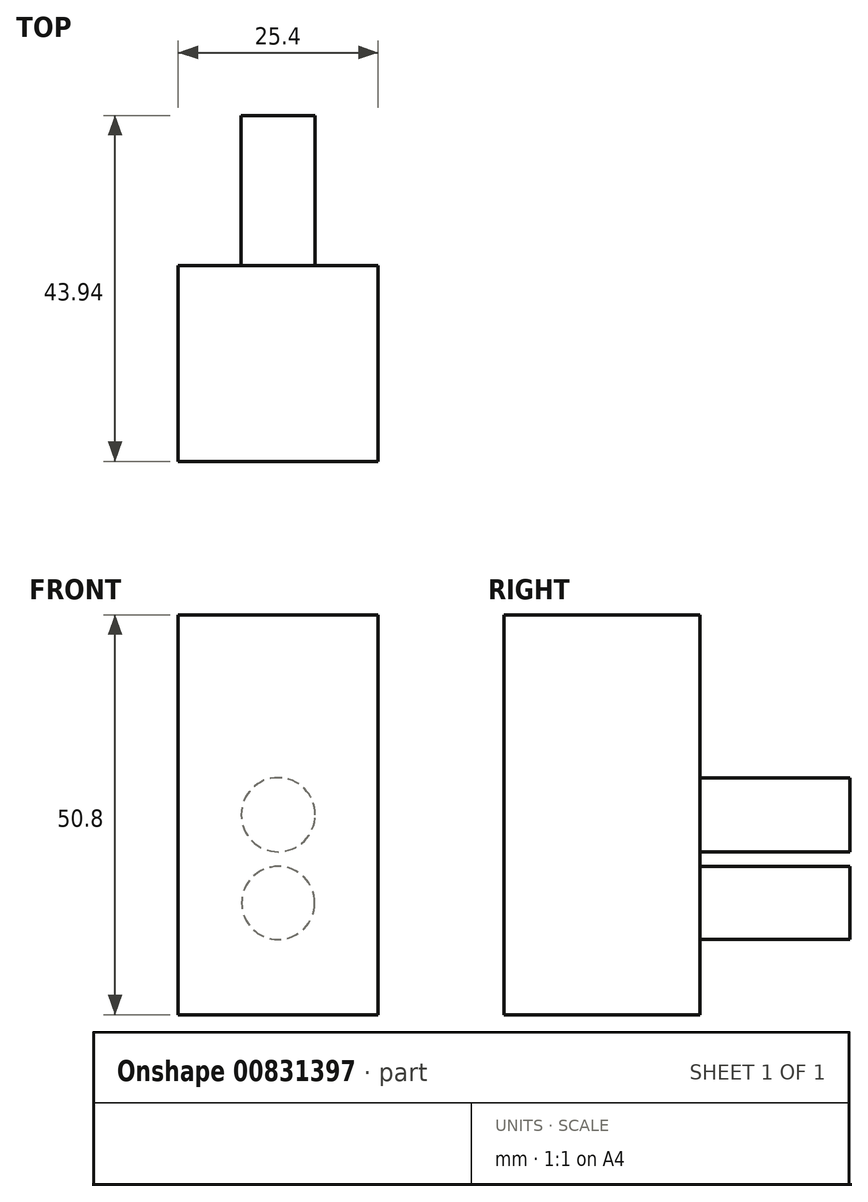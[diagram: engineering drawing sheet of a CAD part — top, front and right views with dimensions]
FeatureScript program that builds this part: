
annotation { "Feature Type Name" : "Feature", "Feature Type Description" : "" }
export const myFeature = defineFeature(function(context is Context, id is Id, definition is map)
    precondition{}
    {
        {
            var Q0;
            Q0=qCreatedBy(makeId("Front.planeOp"),FACE);
            var sketch = newSketch(context, id + "F0", { "sketchPlane" : qUnion([Q0])});
            skLineSegment(sketch, "E0.bottom", {"start": v(12.7, -25.4) * mm, "end": v(-12.7, -25.4) * mm});
            skLineSegment(sketch, "E0.top", {"start": v(12.7, 25.4) * mm, "end": v(-12.7, 25.4) * mm});
            skLineSegment(sketch, "E0.left", {"start": v(12.7, -25.4) * mm, "end": v(12.7, 25.4) * mm});
            skLineSegment(sketch, "E0.right", {"start": v(-12.7, -25.4) * mm, "end": v(-12.7, 25.4) * mm});
            skPoint(sketch, "E0.middle", {"position": v(0, 0) * mm});
            skSolve(sketch);
        }
        {
            var Q0;
            Q0 = qSketchRegion(id + "F0", true);
            var Q1;
            Q1 = qSketchRegion(id + "F2", true);
            extrude(context, id + "F1", {"entities" : qUnion([Q0, Q1]), "depth" : 24.9 * mm, "offsetDistance" : 25.4 * mm});
        }
        {
            var Q0;
            Q0=qCreatedBy(makeId("Front.planeOp"),FACE);
            var sketch = newSketch(context, id + "F2", { "sketchPlane" : qUnion([Q0])});
            skCircle(sketch, "E1", {"center": v(0, 0) * mm, "radius": 4.7 * mm});
            skCircle(sketch, "E2", {"center": v(0, -11.2) * mm, "radius": 4.64 * mm});
            skSolve(sketch);
        }
        {
            var Q0;
            Q0 = qSketchRegion(id + "F2", true);
            extrude(context, id + "F3", {"entities" : qUnion([Q0]), "operationType" : NewBodyOperationType.ADD, "oppositeDirection" : true, "depth" : 19.05 * mm, "offsetDistance" : 25.4 * mm});
        }
    });
